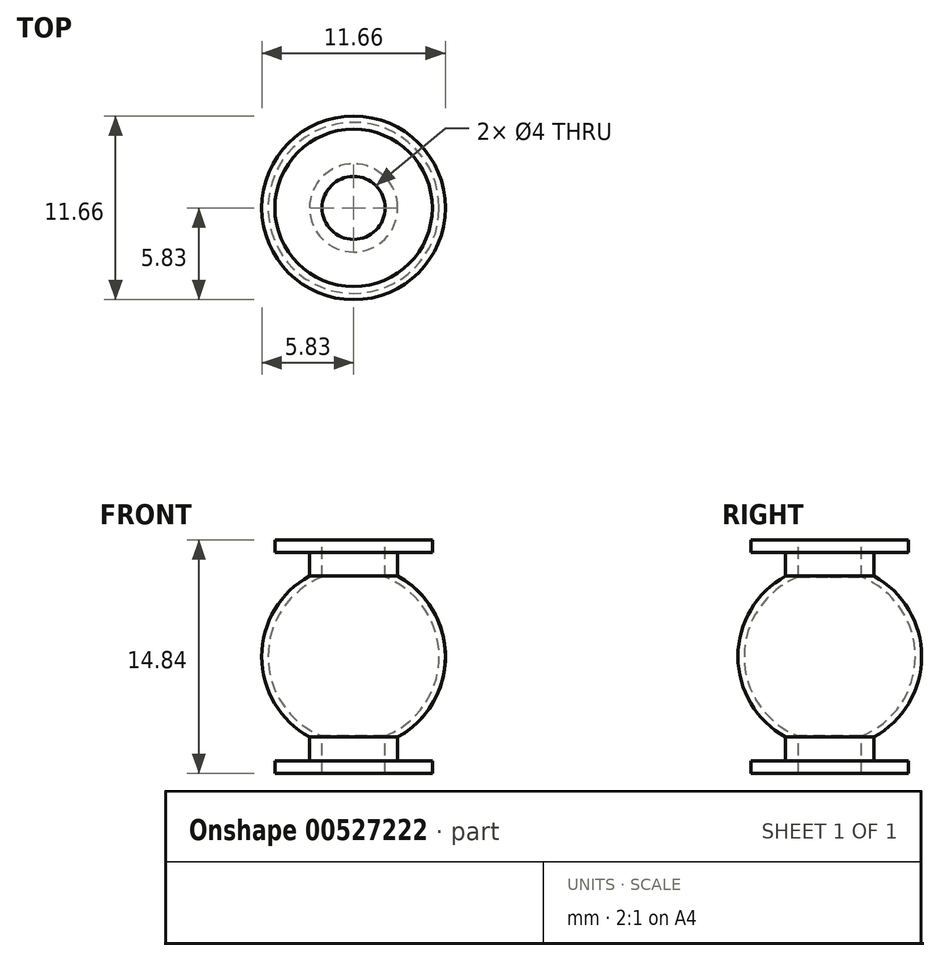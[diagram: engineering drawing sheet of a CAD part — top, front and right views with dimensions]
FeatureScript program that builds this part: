
annotation { "Feature Type Name" : "Feature", "Feature Type Description" : "" }
export const myFeature = defineFeature(function(context is Context, id is Id, definition is map)
    precondition{}
    {
        {
            var Q0;
            Q0=qCreatedBy(makeId("Front.planeOp"),FACE);
            var sketch = newSketch(context, id + "F0", { "sketchPlane" : qUnion([Q0])});
            skLineSegment(sketch, "E0", {"start": v(-2.8, 5.12) * mm, "end": v(-2.8, 6.62) * mm});
            skLineSegment(sketch, "E1", {"start": v(-2.8, 6.62) * mm, "end": v(-5, 6.62) * mm});
            skLineSegment(sketch, "E2", {"start": v(-5, 6.62) * mm, "end": v(-5, 7.42) * mm});
            skLineSegment(sketch, "E3", {"start": v(-5, 7.42) * mm, "end": v(-2, 7.42) * mm});
            skLineSegment(sketch, "E4", {"start": v(-2, 7.42) * mm, "end": v(-2, 5.05) * mm});
            skLineSegment(sketch, "E5.MirrorCS", {"start": v(-2.8, -5.12) * mm, "end": v(-2.8, -6.62) * mm});
            skLineSegment(sketch, "E6.MirrorCS", {"start": v(-2, -7.42) * mm, "end": v(-2, -5.05) * mm});
            skLineSegment(sketch, "E7.MirrorCS", {"start": v(-5, -7.42) * mm, "end": v(-2, -7.42) * mm});
            skLineSegment(sketch, "E8.MirrorCS", {"start": v(-2.8, -6.62) * mm, "end": v(-5, -6.62) * mm});
            skLineSegment(sketch, "E9.MirrorCS", {"start": v(-5, -6.62) * mm, "end": v(-5, -7.42) * mm});
            skLineSegment(sketch, "E10", {"start": v(0, 10.68) * mm, "end": v(0, -11.57) * mm, "construction": true});
            skArc(sketch, "E11", {"start": v(-2.8, 5.12) * mm, "mid": v(-5.83, 0) * mm, "end": v(-2.8, -5.12) * mm});
            skArc(sketch, "E12", {"start": v(-2, 5.05) * mm, "mid": v(-5.43, 0) * mm, "end": v(-2, -5.05) * mm});
            skSolve(sketch);
        }
        {
            var Q0;
            Q0=makeQuery(id+"F0.imprint","IMPRINT",FACE,{"disambiguationData":[TD([[makeQuery(id+"F0.imprint","IMPRINT",EDGE,{"derivedFrom":sQuery(id+"F0.wireOp",EDGE,"E0")}),-1.0]])]});
            var Q1;
            Q1=sQuery(id+"F0.wireOp",EDGE,"E10");
            revolve(context, id + "F1", {"entities" : qUnion([Q0]), "axis" : qUnion([Q1]), "revolveType" : RevolveType.FULL});
        }
    });
